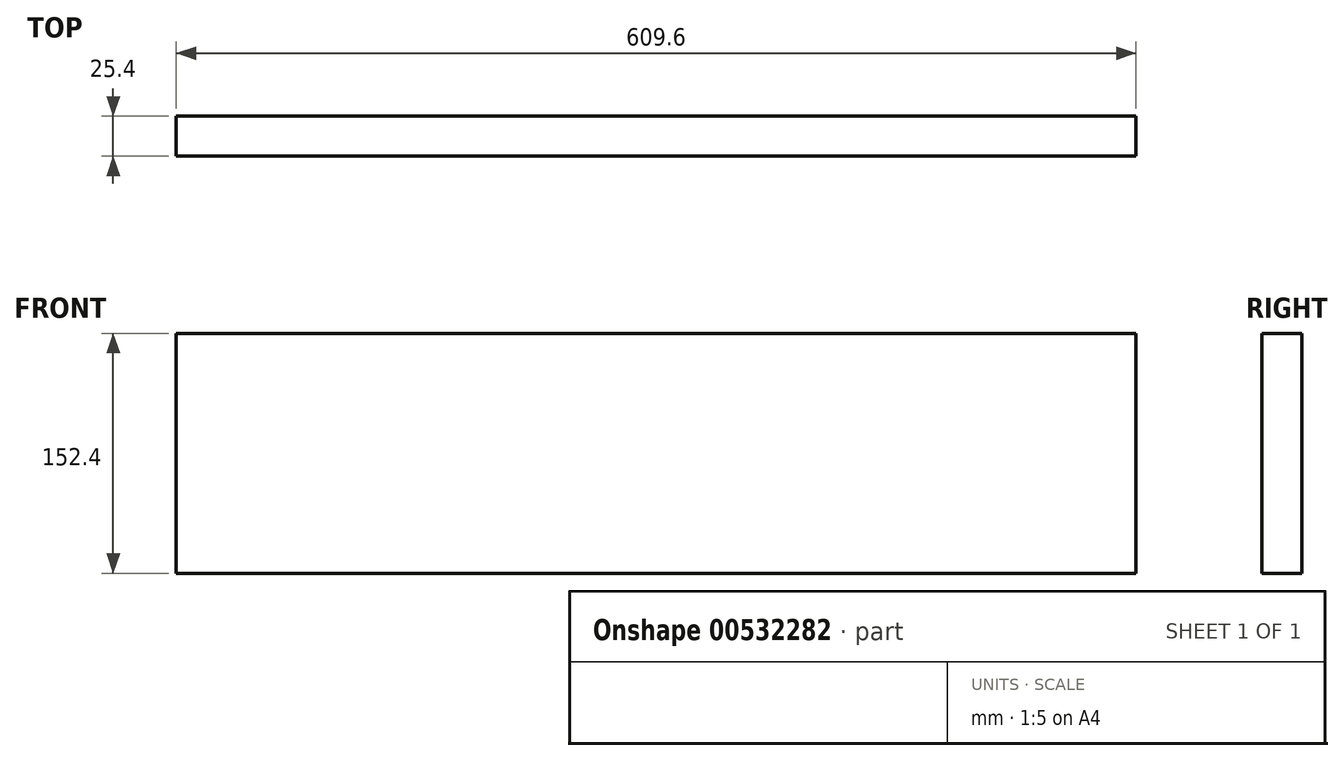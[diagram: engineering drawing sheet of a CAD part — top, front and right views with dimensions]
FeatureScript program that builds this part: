
annotation { "Feature Type Name" : "Feature", "Feature Type Description" : "" }
export const myFeature = defineFeature(function(context is Context, id is Id, definition is map)
    precondition{}
    {
        {
            var Q0;
            Q0=qCreatedBy(makeId("Front.planeOp"),FACE);
            var sketch = newSketch(context, id + "F0", { "sketchPlane" : qUnion([Q0])});
            skLineSegment(sketch, "E0.bottom", {"start": v(0, 0) * mm, "end": v(609.6, 0) * mm});
            skLineSegment(sketch, "E0.top", {"start": v(0, 152.4) * mm, "end": v(609.6, 152.4) * mm});
            skLineSegment(sketch, "E0.left", {"start": v(0, 0) * mm, "end": v(0, 152.4) * mm});
            skLineSegment(sketch, "E0.right", {"start": v(609.6, 0) * mm, "end": v(609.6, 152.4) * mm});
            skSolve(sketch);
        }
        {
            var Q0;
            Q0=makeQuery(id+"F0.imprint","IMPRINT",FACE,{"disambiguationData":[TD([[makeQuery(id+"F0.imprint","IMPRINT",EDGE,{"derivedFrom":sQuery(id+"F0.wireOp",EDGE,"E0.bottom")}),1.0]])]});
            extrude(context, id + "F1", {"entities" : qUnion([Q0]), "depth" : 25.4 * mm, "offsetDistance" : 25.4 * mm});
        }
    });
